# Revit family: Sigur
name_source: partatom
category: Furniture
revit_build: Autodesk Revit 2015 (Build: 20140606_1530(x64)
units: mm (PartAtom-declared; Revit-internal decimal feet)

## types (6) — shared parameters
Manufacturer = Isku Oy
Type Comments = Available as antimicrobial
URL = www.isku.fi

## per-type parameters (varying)
| type | Armrest | Width |
| Sigur 3744 width 630 mm with armrest | Yes | 566 mm  [stored 1.85696 ft] |
| Sigur 3744 width 1230 mm with armrest | Yes | 1166 mm  [stored 3.82546 ft] |
| Sigur 3744 width 1820 mm with armrest | Yes | 1756 mm  [stored 5.76115 ft] |
| Sigur 3744 width 1820 mm no armrest | No | 1756 mm  [stored 5.76115 ft] |
| Sigur 3744 width 1230 mm no armrest | No | 1166 mm  [stored 3.82546 ft] |
| Sigur 3744 width 630 mm no armrest | No | 566 mm  [stored 1.85696 ft] |

note: [stored X ft] marks values corroborated as IEEE doubles in the binary element streams (Revit-internal decimal feet)

## geometry (parser evidence)
native form markers: Sweep x5
no freeform markers — native parametric forms only
